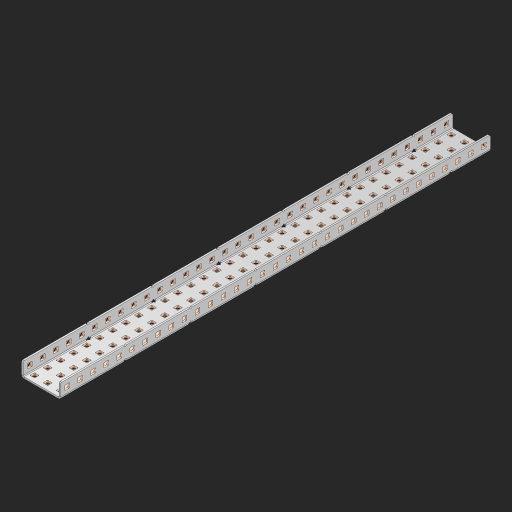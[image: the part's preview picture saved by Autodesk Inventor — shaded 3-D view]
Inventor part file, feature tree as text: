
AUTODESK INVENTOR PART (.ipt)
format: ipt  version: 2023 (Build 270158000, 158)  size: 1,954,816 bytes
history: native  units: in
note: dims shown in document units (in); Inventor stores cm internally (conversion verified against a paired STEP export)
features: other x170, extrude x164, sheet_metal_op x10, sketch x8, mirror x1, pattern_linear x1, chamfer x1
ambient origin geometry x8: Origin, YZ Plane, XZ Plane, XY Plane, X Axis, Y Axis, Z Axis, Center Point
bodies: Solid1 (feature_tree), Body (feature_tree)
feature tree (355):
  other  "Flange Pattern Plane"
  sheet_metal_op  "Flange Pattern"
  sheet_metal_op  "Body Pattern"
  other  "Arc Length"
  mirror  "Notch Mirror"
  pattern_linear  "Notch Pattern"  Spacing1=0.25in  [1 undecoded]
  chamfer  "End Chamfer"
  extrude  "Half Cut"  Depth=0.0625in
  sketch  "Sketch1"  dims[d0=1.5in]
  other  "Plate1"
  sketch  "Sketch2"  dims[d1=16.5in]
  other  "Plate2"
  sheet_metal_op  "Bend1"
  sheet_metal_op  "Corner1"
  sketch  "Sketch3"  dims[d2=0.0625in]
  other  "Flange Pattern Sketch"
  sketch  "Sketch7"  dims[d3=0.0625in]
  other  "Srf1"
  other  "Srf2"
  sketch  "Sketch8"  dims[d4=0.0312in]
  sketch  "Sketch9"  dims[d5=0.125in]
  other  "Srf91"
  sheet_metal_op  "Body Pattern Sketch"
  other  "Srf92"
  sketch  "Sketch13"  dims[d6=0.0625in]
  sketch  "Sketch14"  dims[d7=0.5in d8=90.0deg d9=0.0312in d10=0.25in d11=0.0625in d12=0.0625in d16=0.182in d17=0.02in d18=0.0625in d19=0.0in d20=0.25in d21=0.25in d46=0.172in d47=1.0in d48=0.0in d49=0.182in d50=0.02in d51=0.25in d52=0.25in d53=0.0625in d54=0.0in d55=0.172in d56=1.0in d57=0.0in d60=12.9921in d62=0.5in d63=1.1811in d65=0.5in d85=0.1473in d86=0.1782in d88=0.04in d89=0.0625in d90=0.0in d91=0.04in d92=0.0491in d95=2.5in d96=0.04in d97=0.25in d98=45.0deg d101=0.0in d102=2.497in d131=1.5in d132=12.9921in d134=0.5in d139=0.5in]
  other  "Srf856"
  other  "Srf1310"
  other  "Srf1311"
  other  "Srf1312"
  other  "Srf1376"
  other  "Srf1377"
  other  "Srf1728"
  other  "Srf1755"
  other  "Srf1878"
  other  "Srf1879"
  other  "Srf1880"
  other  "Srf1881"
  other  "Srf1882"
  other  "Srf1883"
  other  "Srf1884"
  other  "Srf1885"
  other  "Srf1886"
  other  "Srf1887"
  other  "Srf1888"
  other  "Srf1889"
  other  "Srf1890"
  other  "Srf1891"
  other  "Srf1892"
  other  "Srf1893"
  other  "Srf1894"
  other  "Srf1895"
  other  "Srf1896"
  other  "Srf1897"
  other  "Srf1898"
  other  "Srf1899"
  other  "Srf1900"
  other  "Srf1901"
  other  "Srf1902"
  other  "Srf1903"
  other  "Srf1904"
  other  "Srf1905"
  other  "Srf1906"
  other  "Srf1907"
  other  "Srf1908"
  other  "Srf1909"
  other  "Srf1910"
  other  "Srf1911"
  other  "Srf1912"
  other  "Srf1913"
  other  "Srf1914"
  other  "Srf1915"
  other  "Srf1916"
  other  "Srf1917"
  other  "Srf1918"
  other  "Srf1919"
  other  "Srf1920"
  other  "Srf1921"
  other  "Srf1922"
  other  "Srf1923"
  other  "Srf1924"
  other  "Srf1925"
  other  "Srf1926"
  other  "Srf1927"
  other  "Srf1928"
  other  "Srf1929"
  other  "Srf1930"
  other  "Srf1931"
  other  "Srf1932"
  other  "Srf1933"
  other  "Srf1934"
  other  "Srf1935"
  other  "Srf1936"
  other  "Srf1937"
  other  "Srf1942"
  other  "Srf1943"
  other  "Srf1944"
  other  "Srf1945"
  other  "Srf1946"
  other  "Srf1947"
  other  "Srf1948"
  other  "Srf1949"
  other  "Srf1950"
  other  "Srf1951"
  other  "Srf1952"
  other  "Srf1953"
  other  "Srf1954"
  other  "Srf1955"
  other  "Srf1956"
  other  "Srf1957"
  other  "Srf1958"
  other  "Srf1959"
  other  "Srf1960"
  other  "Srf1961"
  other  "Srf1962"
  other  "Srf1963"
  other  "Srf1964"
  other  "Srf1965"
  other  "Srf1966"
  other  "Srf1967"
  other  "Srf1968"
  other  "Srf1969"
  other  "Srf1970"
  other  "Srf1971"
  other  "Srf1972"
  other  "Srf1973"
  other  "Srf1974"
  other  "Srf1975"
  other  "Srf1976"
  other  "Srf1977"
  other  "Srf1978"
  other  "Srf1979"
  other  "Srf1980"
  other  "Srf1981"
  other  "Srf1982"
  other  "Srf1983"
  other  "Srf1984"
  other  "Srf1985"
  other  "Srf1986"
  other  "Srf1987"
  other  "Srf1988"
  other  "Srf1989"
  other  "Srf1990"
  other  "Srf1991"
  other  "Srf1992"
  other  "Srf1993"
  other  "Srf1994"
  other  "Srf1995"
  other  "Srf1996"
  other  "Srf1997"
  other  "Srf1998"
  other  "Srf1999"
  other  "Srf2000"
  other  "Srf2001"
  other  "Srf2002"
  other  "Srf2003"
  other  "Srf2004"
  other  "Srf2005"
  other  "Srf2006"
  other  "Srf2007"
  other  "Srf2008"
  other  "Srf2009"
  other  "Srf2010"
  other  "Srf2011"
  other  "Srf2012"
  other  "Srf2013"
  other  "Srf2014"
  other  "Srf2015"
  other  "Srf2016"
  other  "Srf2017"
  other  "Srf2018"
  other  "Srf2019"
  other  "Srf2020"
  other  "Srf2021"
  other  "Srf2022"
  other  "Srf2023"
  other  "Srf2024"
  other  "Srf2025"
  other  "Srf2026"
  other  "Srf2027"
  other  "Srf2028"
  other  "Srf2029"
  other  "Srf2030"
  other  "Srf2031"
  other  "Srf2032"
  other  "Srf2033"
  other  "Srf2034"
  sheet_metal_op  "Flange Stamp"
  sheet_metal_op  "Flange Circle"
  sheet_metal_op  "Body Stamp"
  sheet_metal_op  "Body Circle"
  sheet_metal_op  "Notch"
  extrude  "ExtrusionSrf2"  Depth=0.0625in
  extrude  "ExtrusionSrf92"  Depth=1.5in
  extrude  "ExtrusionSrf856"  Depth=0.02in
  extrude  "ExtrusionSrf1310"  Depth=0.0625in
  extrude  "ExtrusionSrf1311"  TaperAngle=0.0deg  [1 undecoded]
  extrude  "ExtrusionSrf1312"  Depth=0.25in
  extrude  "ExtrusionSrf1376"  Depth=0.25in
  extrude  "ExtrusionSrf1377"  Depth=1.5in
  extrude  "ExtrusionSrf1728"  Depth=1.5in TaperAngle=0.0deg
  extrude  "ExtrusionSrf1755"  Depth=1.5in
  extrude  "ExtrusionSrf1878"  Depth=0.02in
  extrude  "ExtrusionSrf1879"  Depth=0.25in
  extrude  "ExtrusionSrf1880"  Depth=0.25in
  extrude  "ExtrusionSrf1881"  Depth=0.0625in
  extrude  "ExtrusionSrf1882"  TaperAngle=0.0deg  [1 undecoded]
  extrude  "ExtrusionSrf1883"  Depth=1.5in
  extrude  "ExtrusionSrf1884"  Depth=1.5in TaperAngle=0.0deg
  extrude  "ExtrusionSrf1885"  Depth=1.5in
  extrude  "ExtrusionSrf1886"  Depth=1.5in
  extrude  "ExtrusionSrf1887"  Depth=1.5in
  extrude  "ExtrusionSrf1888"  Depth=1.5in
  extrude  "ExtrusionSrf1889"  Depth=1.5in
  extrude  "ExtrusionSrf1890"  Depth=0.0625in
  extrude  "ExtrusionSrf1891"  TaperAngle=0.0deg  [1 undecoded]
  extrude  "ExtrusionSrf1892"  Depth=1.5in
  extrude  "ExtrusionSrf1893"  Depth=1.5in
  extrude  "ExtrusionSrf1894"  Depth=1.5in
  extrude  "ExtrusionSrf1895"  Depth=0.25in TaperAngle=45.0deg
  extrude  "ExtrusionSrf1896"  TaperAngle=0.0deg  [1 undecoded]
  extrude  "ExtrusionSrf1897"  Depth=1.5in
  extrude  "ExtrusionSrf1898"  Depth=1.5in
  extrude  "ExtrusionSrf1899"  Depth=1.5in
  extrude  "ExtrusionSrf1900"  Depth=1.5in
  extrude  "ExtrusionSrf1901"  Depth=1.5in
  extrude  "ExtrusionSrf1902"  [1 undecoded]
  extrude  "ExtrusionSrf1903"  [1 undecoded]
  extrude  "ExtrusionSrf1904"  [1 undecoded]
  extrude  "ExtrusionSrf1905"  [1 undecoded]
  extrude  "ExtrusionSrf1906"  [1 undecoded]
  extrude  "ExtrusionSrf1907"  [1 undecoded]
  extrude  "ExtrusionSrf1908"  [1 undecoded]
  extrude  "ExtrusionSrf1909"  [1 undecoded]
  extrude  "ExtrusionSrf1910"  [1 undecoded]
  extrude  "ExtrusionSrf1911"  [1 undecoded]
  extrude  "ExtrusionSrf1912"  [1 undecoded]
  extrude  "ExtrusionSrf1913"  [1 undecoded]
  extrude  "ExtrusionSrf1914"  [1 undecoded]
  extrude  "ExtrusionSrf1915"  [1 undecoded]
  extrude  "ExtrusionSrf1916"  [1 undecoded]
  extrude  "ExtrusionSrf1917"  [1 undecoded]
  extrude  "ExtrusionSrf1918"  [1 undecoded]
  extrude  "ExtrusionSrf1919"  [1 undecoded]
  extrude  "ExtrusionSrf1920"  [1 undecoded]
  extrude  "ExtrusionSrf1921"  [1 undecoded]
  extrude  "ExtrusionSrf1922"  [1 undecoded]
  extrude  "ExtrusionSrf1923"  [1 undecoded]
  extrude  "ExtrusionSrf1924"  [1 undecoded]
  extrude  "ExtrusionSrf1925"  [1 undecoded]
  extrude  "ExtrusionSrf1926"  [1 undecoded]
  extrude  "ExtrusionSrf1927"  [1 undecoded]
  extrude  "ExtrusionSrf1928"  [1 undecoded]
  extrude  "ExtrusionSrf1929"  [1 undecoded]
  extrude  "ExtrusionSrf1930"  [1 undecoded]
  extrude  "ExtrusionSrf1931"  [1 undecoded]
  extrude  "ExtrusionSrf1932"  [1 undecoded]
  extrude  "ExtrusionSrf1933"  [1 undecoded]
  extrude  "ExtrusionSrf1934"  [1 undecoded]
  extrude  "ExtrusionSrf1935"  [1 undecoded]
  extrude  "ExtrusionSrf1936"  [1 undecoded]
  extrude  "ExtrusionSrf1937"  [1 undecoded]
  extrude  "ExtrusionSrf1942"  [1 undecoded]
  extrude  "ExtrusionSrf1943"  [1 undecoded]
  extrude  "ExtrusionSrf1944"  [1 undecoded]
  extrude  "ExtrusionSrf1945"  [1 undecoded]
  extrude  "ExtrusionSrf1946"  [1 undecoded]
  extrude  "ExtrusionSrf1947"  [1 undecoded]
  extrude  "ExtrusionSrf1948"  [1 undecoded]
  extrude  "ExtrusionSrf1949"  [1 undecoded]
  extrude  "ExtrusionSrf1950"  [1 undecoded]
  extrude  "ExtrusionSrf1951"  [1 undecoded]
  extrude  "ExtrusionSrf1952"  [1 undecoded]
  extrude  "ExtrusionSrf1953"  [1 undecoded]
  extrude  "ExtrusionSrf1954"  [1 undecoded]
  extrude  "ExtrusionSrf1955"  [1 undecoded]
  extrude  "ExtrusionSrf1956"  [1 undecoded]
  extrude  "ExtrusionSrf1957"  [1 undecoded]
  extrude  "ExtrusionSrf1958"  [1 undecoded]
  extrude  "ExtrusionSrf1959"  [1 undecoded]
  extrude  "ExtrusionSrf1960"  [1 undecoded]
  extrude  "ExtrusionSrf1961"  [1 undecoded]
  extrude  "ExtrusionSrf1962"  [1 undecoded]
  extrude  "ExtrusionSrf1963"  [1 undecoded]
  extrude  "ExtrusionSrf1964"  [1 undecoded]
  extrude  "ExtrusionSrf1965"  [1 undecoded]
  extrude  "ExtrusionSrf1966"  [1 undecoded]
  extrude  "ExtrusionSrf1967"  [1 undecoded]
  extrude  "ExtrusionSrf1968"  [1 undecoded]
  extrude  "ExtrusionSrf1969"  [1 undecoded]
  extrude  "ExtrusionSrf1970"  [1 undecoded]
  extrude  "ExtrusionSrf1971"  [1 undecoded]
  extrude  "ExtrusionSrf1972"  [1 undecoded]
  extrude  "ExtrusionSrf1973"  [1 undecoded]
  extrude  "ExtrusionSrf1974"  [1 undecoded]
  extrude  "ExtrusionSrf1975"  [1 undecoded]
  extrude  "ExtrusionSrf1976"  [1 undecoded]
  extrude  "ExtrusionSrf1977"  [1 undecoded]
  extrude  "ExtrusionSrf1978"  [1 undecoded]
  extrude  "ExtrusionSrf1979"  [1 undecoded]
  extrude  "ExtrusionSrf1980"  [1 undecoded]
  extrude  "ExtrusionSrf1981"  [1 undecoded]
  extrude  "ExtrusionSrf1982"  [1 undecoded]
  extrude  "ExtrusionSrf1983"  [1 undecoded]
  extrude  "ExtrusionSrf1984"  [1 undecoded]
  extrude  "ExtrusionSrf1985"  [1 undecoded]
  extrude  "ExtrusionSrf1986"  [1 undecoded]
  extrude  "ExtrusionSrf1987"  [1 undecoded]
  extrude  "ExtrusionSrf1988"  [1 undecoded]
  extrude  "ExtrusionSrf1989"  [1 undecoded]
  extrude  "ExtrusionSrf1990"  [1 undecoded]
  extrude  "ExtrusionSrf1991"  [1 undecoded]
  extrude  "ExtrusionSrf1992"  [1 undecoded]
  extrude  "ExtrusionSrf1993"  [1 undecoded]
  extrude  "ExtrusionSrf1994"  [1 undecoded]
  extrude  "ExtrusionSrf1995"  [1 undecoded]
  extrude  "ExtrusionSrf1996"  [1 undecoded]
  extrude  "ExtrusionSrf1997"  [1 undecoded]
  extrude  "ExtrusionSrf1998"  [1 undecoded]
  extrude  "ExtrusionSrf1999"  [1 undecoded]
  extrude  "ExtrusionSrf2000"  [1 undecoded]
  extrude  "ExtrusionSrf2001"  [1 undecoded]
  extrude  "ExtrusionSrf2002"  [1 undecoded]
  extrude  "ExtrusionSrf2003"  [1 undecoded]
  extrude  "ExtrusionSrf2004"  [1 undecoded]
  extrude  "ExtrusionSrf2005"  [1 undecoded]
  extrude  "ExtrusionSrf2006"  [1 undecoded]
  extrude  "ExtrusionSrf2007"  [1 undecoded]
  extrude  "ExtrusionSrf2008"  [1 undecoded]
  extrude  "ExtrusionSrf2009"  [1 undecoded]
  extrude  "ExtrusionSrf2010"  [1 undecoded]
  extrude  "ExtrusionSrf2011"  [1 undecoded]
  extrude  "ExtrusionSrf2012"  [1 undecoded]
  extrude  "ExtrusionSrf2013"  [1 undecoded]
  extrude  "ExtrusionSrf2014"  [1 undecoded]
  extrude  "ExtrusionSrf2015"  [1 undecoded]
  extrude  "ExtrusionSrf2016"  [1 undecoded]
  extrude  "ExtrusionSrf2017"  [1 undecoded]
  extrude  "ExtrusionSrf2018"  [1 undecoded]
  extrude  "ExtrusionSrf2019"  [1 undecoded]
  extrude  "ExtrusionSrf2020"  [1 undecoded]
  extrude  "ExtrusionSrf2021"  [1 undecoded]
  extrude  "ExtrusionSrf2022"  [1 undecoded]
  extrude  "ExtrusionSrf2023"  [1 undecoded]
  extrude  "ExtrusionSrf2024"  [1 undecoded]
  extrude  "ExtrusionSrf2025"  [1 undecoded]
  extrude  "ExtrusionSrf2026"  [1 undecoded]
  extrude  "ExtrusionSrf2027"  [1 undecoded]
  extrude  "ExtrusionSrf2028"  [1 undecoded]
  extrude  "ExtrusionSrf2029"  [1 undecoded]
  extrude  "ExtrusionSrf2030"  [1 undecoded]
  extrude  "ExtrusionSrf2031"  [1 undecoded]
  extrude  "ExtrusionSrf2032"  [1 undecoded]
  extrude  "ExtrusionSrf2033"  [1 undecoded]
  extrude  "ExtrusionSrf2034"  [1 undecoded]
note: 134 required parameter values undecoded (feature->parameter linkage not recoverable at this tier; creation-order binding heuristic only, values carry confidence <= 0.55)
